# Revit family: 531_OXAT_1-DBF_nailfin
name_source: partatom
category: Windows
units: mm (PartAtom-declared; Revit-internal decimal feet)

## family parameters
Always vertical = Yes
Cut with Voids When Loaded = No
Host = Wall
OmniClass Number = 23.30.20.00
OmniClass Title = Windows
Room Calculation Point = No
Shared = No

## types (112) — shared parameters
Default Sill Height = 31 1/2"
Wall Closure = By host

## per-type parameters (varying)
| type | HBS | Height | MLW1 | MLW2 | Vbs | Width |
| 48x36 | 18" | 36" | 3" | 2 1/4" | 24" | 48" |
| 72x60 | 30" | 60" | 4 1/2" | 3 3/4" | 36" | 72" |
| 24x24Min | 12" | 24" | 1 1/2" | 1 1/2" | 12" | 24" |
| 96x96Max | 48" | 96" | 4 1/2" | 6" | 36" | 96" |
| 36x36 | 18" | 36" | 2 1/4" | 2 1/4" | 18" | 36" |
| 60x60 | 30" | 60" | 3 3/4" | 3 3/4" | 30" | 60" |
| 84x84 | 42" | 84" | 4 1/2" | 5 1/4" | 36" | 84" |
| 24x30 | 15" | 30" | 1 1/2" | 1 7/8" | 12" | 24" |
| 24x36 | 18" | 36" | 1 1/2" | 2 1/4" | 12" | 24" |
| 24x42 | 21" | 42" | 1 1/2" | 2 5/8" | 12" | 24" |
| 24x48 | 24" | 48" | 1 1/2" | 3" | 12" | 24" |
| 24x54 | 24" | 54" | 1 1/2" | 3 3/4" | 12" | 24" |
| 30x24 | 12" | 24" | 1 7/8" | 1 1/2" | 15" | 30" |
| 30x30 | 12" | 30" | 1 7/8" | 2 1/4" | 15" | 30" |
| 30x36 | 18" | 36" | 1 7/8" | 2 1/4" | 15" | 30" |
| 30x42 | 18" | 42" | 1 7/8" | 3" | 15" | 30" |
| 30x48 | 24" | 48" | 1 7/8" | 3" | 15" | 30" |
| 30x60 | 30" | 60" | 1 7/8" | 3 3/4" | 15" | 30" |
| 30x54 | 24" | 54" | 1 7/8" | 3 3/4" | 15" | 30" |
| 36x24 | 12" | 24" | 2 1/4" | 1 1/2" | 18" | 36" |
| 36x30 | 12" | 30" | 2 1/4" | 2 1/4" | 18" | 36" |
| 36x42 | 18" | 42" | 2 1/4" | 3" | 18" | 36" |
| 36x48 | 24" | 48" | 2 1/4" | 3" | 18" | 36" |
| 36x54 | 24" | 54" | 2 1/4" | 3 3/4" | 18" | 36" |
| 36x60 | 30" | 60" | 2 1/4" | 3 3/4" | 18" | 36" |
| 36x66 | 30" | 66" | 2 1/4" | 4 1/2" | 18" | 36" |
| 36x72 | 36" | 72" | 2 1/4" | 4 1/2" | 18" | 36" |
| 42x30 | 15" | 30" | 2 5/8" | 1 7/8" | 21" | 42" |
| 42x36 | 18" | 36" | 2 5/8" | 2 1/4" | 21" | 42" |
| 42x42 | 18" | 42" | 2 5/8" | 3" | 21" | 42" |
| 42x48 | 24" | 48" | 2 5/8" | 3" | 21" | 42" |
| 42x54 | 24" | 54" | 2 5/8" | 3 3/4" | 21" | 42" |
| 42x60 | 30" | 60" | 2 5/8" | 3 3/4" | 21" | 42" |
| 42x66 | 30" | 66" | 2 5/8" | 4 1/2" | 21" | 42" |
| 42x72 | 36" | 72" | 2 5/8" | 4 1/2" | 21" | 42" |
| 48x42 | 18" | 42" | 3" | 3" | 24" | 48" |
| 48x48 | 24" | 48" | 3" | 3" | 24" | 48" |
| 48x54 | 24" | 54" | 3" | 3 3/4" | 24" | 48" |
| 48x60 | 30" | 60" | 3" | 3 3/4" | 24" | 48" |
| 48x66 | 30" | 66" | 3" | 4 1/2" | 24" | 48" |
| 48x72 | 36" | 72" | 3" | 4 1/2" | 24" | 48" |
| 48x78 | 36" | 78" | 3" | 5 1/4" | 24" | 48" |
| 54x36 | 18" | 36" | 3 3/8" | 2 1/4" | 27" | 54" |
| 54x42 | 18" | 42" | 3 3/8" | 3" | 27" | 54" |
| 54x48 | 24" | 48" | 3 3/8" | 3" | 27" | 54" |
| 54x54 | 24" | 54" | 3 3/8" | 3 3/4" | 27" | 54" |
| 54x60 | 30" | 60" | 3 3/8" | 3 3/4" | 27" | 54" |
| 54x66 | 30" | 66" | 3 3/8" | 4 1/2" | 27" | 54" |
| 54x72 | 36" | 72" | 3 3/8" | 4 1/2" | 27" | 54" |
| 54x78 | 36" | 78" | 3 3/8" | 5 1/4" | 27" | 54" |
| 54x84 | 42" | 84" | 3 3/8" | 5 1/4" | 27" | 54" |
| 60x42 | 18" | 42" | 3 3/4" | 3" | 30" | 60" |
| 60x48 | 24" | 48" | 3 3/4" | 3" | 30" | 60" |
| 60x54 | 24" | 54" | 3 3/4" | 3 3/4" | 30" | 60" |
| 60x66 | 30" | 66" | 3 3/4" | 4 1/2" | 30" | 60" |
| 60x72 | 36" | 72" | 3 3/4" | 4 1/2" | 30" | 60" |
| 60x78 | 36" | 78" | 3 3/4" | 5 1/4" | 30" | 60" |
| 60x84 | 42" | 84" | 3 3/4" | 5 1/4" | 30" | 60" |
| 60x90 | 42" | 90" | 3 3/4" | 6" | 30" | 60" |
| 66x42 | 18" | 42" | 4 1/8" | 3" | 33" | 66" |
| 66x48 | 24" | 48" | 4 1/8" | 3" | 33" | 66" |
| 66x54 | 24" | 54" | 4 1/8" | 3 3/4" | 33" | 66" |
| 66x60 | 30" | 60" | 4 1/8" | 3 3/4" | 33" | 66" |
| 66x66 | 30" | 66" | 4 1/8" | 4 1/2" | 33" | 66" |
| 66x72 | 36" | 72" | 4 1/8" | 4 1/2" | 33" | 66" |
| 66x78 | 36" | 78" | 4 1/8" | 5 1/4" | 33" | 66" |
| 66x84 | 42" | 84" | 4 1/8" | 5 1/4" | 33" | 66" |
| 66x90 | 42" | 90" | 4 1/8" | 6" | 33" | 66" |
| 66x96 | 48" | 96" | 4 1/8" | 6" | 33" | 66" |
| 72x48 | 24" | 48" | 4 1/2" | 3" | 36" | 72" |
| 72x54 | 24" | 54" | 4 1/2" | 3 3/4" | 36" | 72" |
| 72x66 | 30" | 66" | 4 1/2" | 4 1/2" | 36" | 72" |
| 72x72 | 36" | 72" | 4 1/2" | 4 1/2" | 36" | 72" |
| 72x78 | 36" | 78" | 4 1/2" | 5 1/4" | 36" | 72" |
| 72x84 | 42" | 84" | 4 1/2" | 5 1/4" | 36" | 72" |
| 72x90 | 42" | 90" | 4 1/2" | 6" | 36" | 72" |
| 72x96 | 48" | 96" | 4 1/2" | 6" | 36" | 72" |
| 78x48 | 24" | 48" | 4 1/2" | 3" | 36" | 78" |
| 78x54 | 24" | 54" | 4 1/2" | 3 3/4" | 36" | 78" |
| 78x60 | 30" | 60" | 4 1/2" | 3 3/4" | 36" | 78" |
| 78x66 | 30" | 66" | 4 1/2" | 4 1/2" | 36" | 78" |
| 78x72 | 36" | 72" | 4 1/2" | 4 1/2" | 36" | 78" |
| 78x78 | 36" | 78" | 4 1/2" | 5 1/4" | 36" | 78" |
| 78x84 | 42" | 84" | 4 1/2" | 5 1/4" | 36" | 78" |
| 78x90 | 42" | 90" | 4 1/2" | 6" | 36" | 78" |
| 78x96 | 48" | 96" | 4 1/2" | 6" | 36" | 78" |
| 84x42 | 18" | 42" | 4 1/2" | 3" | 36" | 84" |
| 84x48 | 24" | 48" | 4 1/2" | 3" | 36" | 84" |
| 84x54 | 24" | 54" | 4 1/2" | 3 3/4" | 36" | 84" |
| 84x60 | 30" | 60" | 4 1/2" | 3 3/4" | 36" | 84" |
| 84x66 | 30" | 66" | 4 1/2" | 4 1/2" | 36" | 84" |
| 84x72 | 36" | 72" | 4 1/2" | 4 1/2" | 36" | 84" |
| 84x78 | 36" | 78" | 4 1/2" | 5 1/4" | 36" | 84" |
| 84x90 | 42" | 90" | 4 1/2" | 6" | 36" | 84" |
| 84x96 | 48" | 96" | 4 1/2" | 6" | 36" | 84" |
| 90x48 | 24" | 48" | 4 1/2" | 3" | 36" | 90" |
| 90x54 | 24" | 54" | 4 1/2" | 3 3/4" | 36" | 90" |
| 90x60 | 30" | 60" | 4 1/2" | 3 3/4" | 36" | 90" |
| 90x66 | 30" | 66" | 4 1/2" | 4 1/2" | 36" | 90" |
| 90x72 | 36" | 72" | 4 1/2" | 4 1/2" | 36" | 90" |
| 90x78 | 36" | 78" | 4 1/2" | 5 1/4" | 36" | 90" |
| 90x84 | 42" | 78" | 4 1/2" | 4 1/2" | 36" | 90" |
| 90x90 | 42" | 90" | 4 1/2" | 6" | 36" | 90" |
| 90x96 | 48" | 96" | 4 1/2" | 6" | 36" | 90" |
| 96x48 | 24" | 48" | 4 1/2" | 3" | 36" | 96" |
| 96x54 | 24" | 54" | 4 1/2" | 3 3/4" | 36" | 96" |
| 96x60 | 30" | 60" | 4 1/2" | 3 3/4" | 36" | 96" |
| 96x66 | 30" | 66" | 4 1/2" | 4 1/2" | 36" | 96" |
| 96x72 | 36" | 72" | 4 1/2" | 4 1/2" | 36" | 96" |
| 96x78 | 36" | 78" | 4 1/2" | 5 1/4" | 36" | 96" |
| 96x84 | 42" | 84" | 4 1/2" | 5 1/4" | 36" | 96" |
| 96x90 | 42" | 90" | 4 1/2" | 6" | 36" | 96" |

## geometry (parser evidence)
native form markers: Sweep x2
no freeform markers — native parametric forms only
